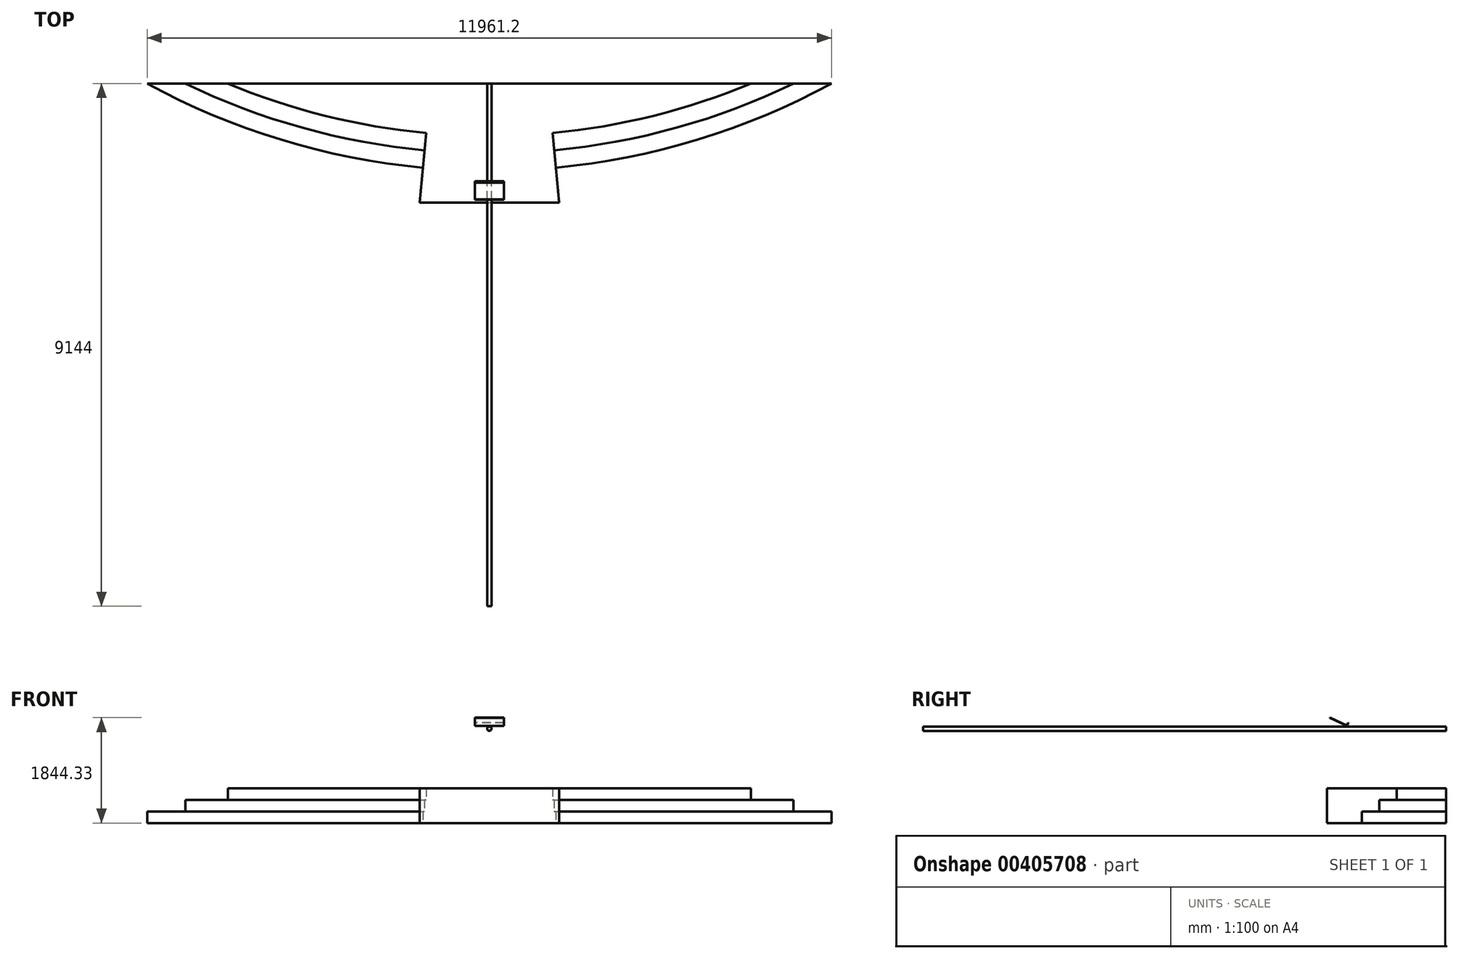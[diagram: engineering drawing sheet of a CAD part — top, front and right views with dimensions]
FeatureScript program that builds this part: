
annotation { "Feature Type Name" : "Feature", "Feature Type Description" : "" }
export const myFeature = defineFeature(function(context is Context, id is Id, definition is map)
    precondition{}
    {
        {
            var Q0;
            Q0=qCreatedBy(makeId("Top.planeOp"),FACE);
            var sketch = newSketch(context, id + "F0", { "sketchPlane" : qUnion([Q0])});
            skLineSegment(sketch, "E0", {"start": v(-4572, 0) * mm, "end": v(4572, 0) * mm});
            skArc(sketch, "E1", {"start": v(-4572, 0) * mm, "mid": v(0, -914.4) * mm, "end": v(4572, 0) * mm});
            skArc(sketch, "E2.0", {"start": v(-5314.37, 0) * mm, "mid": v(0, -1219.2) * mm, "end": v(5314.37, 0) * mm});
            skLineSegment(sketch, "E3", {"start": v(-4572, 0) * mm, "end": v(-5314.37, 0) * mm});
            skLineSegment(sketch, "E4", {"start": v(4572, 0) * mm, "end": v(5314.37, 0) * mm});
            skArc(sketch, "E5.0", {"start": v(-5980.6, 0) * mm, "mid": v(0, -1524) * mm, "end": v(5980.6, 0) * mm});
            skLineSegment(sketch, "E6", {"start": v(-5314.37, 0) * mm, "end": v(-5980.6, 0) * mm});
            skLineSegment(sketch, "E7", {"start": v(5314.37, 0) * mm, "end": v(5980.6, 0) * mm});
            skLineSegment(sketch, "E8", {"start": v(-1105.34, -862.9) * mm, "end": v(-1219.2, -2082.1) * mm});
            skLineSegment(sketch, "E9", {"start": v(-1219.2, -2082.1) * mm, "end": v(1219.2, -2082.1) * mm});
            skLineSegment(sketch, "E10", {"start": v(1219.2, -2082.1) * mm, "end": v(1105.34, -862.9) * mm});
            skLineSegment(sketch, "E11", {"start": v(0, -2082.1) * mm, "end": v(0, -1524) * mm});
            skSolve(sketch);
        }
        {
            var Q0;
            {var subQ0=sQuery(id+"F0.wireOp",EDGE,"E0");Q0=makeQuery(id+"F0.imprint","IMPRINT",FACE,{"disambiguationData":[TD([[makeQuery(id+"F0.imprint","IMPRINT",EDGE,{"derivedFrom":subQ0}),-1.0]])]});}
            var Q1;
            {var subQ0=sQuery(id+"F0.wireOp",EDGE,"E11");Q1=makeQuery(id+"F0.imprint","IMPRINT",FACE,{"disambiguationData":[TD([[makeQuery(id+"F0.imprint","IMPRINT",EDGE,{"derivedFrom":subQ0}),1.0]])]});}
            var Q2;
            {var subQ0=sQuery(id+"F0.wireOp",EDGE,"E11");Q2=makeQuery(id+"F0.imprint","IMPRINT",FACE,{"disambiguationData":[TD([[makeQuery(id+"F0.imprint","IMPRINT",EDGE,{"derivedFrom":subQ0}),-1.0]])]});}
            var Q3;
            {var subQ0=sQuery(id+"F0.wireOp",EDGE,"E8");var subQ3=sQuery(id+"F0.wireOp",EDGE,"E2.0");var subQ4=makeQuery(id+"F0.imprint","INTERSECT",VERTEX,{"derivedFrom":[subQ3,subQ0]});Q3=makeQuery(id+"F0.imprint","IMPRINT",FACE,{"disambiguationData":[TD([[makeQuery(id+"F0.imprint","IMPRINT",EDGE,{"disambiguationData":[TD([[subQ4,-1.0]])],"derivedFrom":subQ3}),-1.0]])]});}
            var Q4;
            {var subQ0=sQuery(id+"F0.wireOp",EDGE,"E8");var subQ1=sQuery(id+"F0.wireOp",EDGE,"E1");var subQ2=makeQuery(id+"F0.imprint","INTERSECT",VERTEX,{"derivedFrom":[subQ1,subQ0]});Q4=makeQuery(id+"F0.imprint","IMPRINT",FACE,{"disambiguationData":[TD([[makeQuery(id+"F0.imprint","IMPRINT",EDGE,{"disambiguationData":[TD([[subQ2,-1.0]])],"derivedFrom":subQ1}),-1.0]])]});}
            extrude(context, id + "F1", {"entities" : qUnion([Q0, Q1, Q2, Q3, Q4]), "depth" : 609.6 * mm});
        }
        {
            var Q0;
            {var subQ0=sQuery(id+"F0.wireOp",EDGE,"E3");Q0=makeQuery(id+"F0.imprint","IMPRINT",FACE,{"disambiguationData":[TD([[makeQuery(id+"F0.imprint","IMPRINT",EDGE,{"derivedFrom":subQ0}),1.0]])]});}
            var Q1;
            {var subQ0=sQuery(id+"F0.wireOp",EDGE,"E4");Q1=makeQuery(id+"F0.imprint","IMPRINT",FACE,{"disambiguationData":[TD([[makeQuery(id+"F0.imprint","IMPRINT",EDGE,{"derivedFrom":subQ0}),-1.0]])]});}
            extrude(context, id + "F2", {"entities" : qUnion([Q0, Q1]), "operationType" : NewBodyOperationType.ADD, "depth" : 406.4 * mm});
        }
        {
            var Q0;
            {var subQ0=sQuery(id+"F0.wireOp",EDGE,"E6");Q0=makeQuery(id+"F0.imprint","IMPRINT",FACE,{"disambiguationData":[TD([[makeQuery(id+"F0.imprint","IMPRINT",EDGE,{"derivedFrom":subQ0}),1.0]])]});}
            var Q1;
            {var subQ0=sQuery(id+"F0.wireOp",EDGE,"E7");Q1=makeQuery(id+"F0.imprint","IMPRINT",FACE,{"disambiguationData":[TD([[makeQuery(id+"F0.imprint","IMPRINT",EDGE,{"derivedFrom":subQ0}),-1.0]])]});}
            extrude(context, id + "F3", {"entities" : qUnion([Q0, Q1]), "operationType" : NewBodyOperationType.ADD, "depth" : 203.2 * mm});
        }
        {
            var Q0;
            Q0=qCreatedBy(makeId("Front.planeOp"),FACE);
            var sketch = newSketch(context, id + "F4", { "sketchPlane" : qUnion([Q0])});
            skLineSegment(sketch, "E12", {"start": v(0, 0) * mm, "end": v(0, 1651) * mm});
            skCircle(sketch, "E13", {"center": v(0, 1651) * mm, "radius": 38.1 * mm});
            skSolve(sketch);
        }
        {
            var Q0;
            Q0 = qSketchRegion(id + "F4", true);
            extrude(context, id + "F5", {"entities" : qUnion([Q0]), "depth" : 9144 * mm});
        }
        {
            var Q0;
            Q0=qCreatedBy(makeId("Right.planeOp"),FACE);
            var sketch = newSketch(context, id + "F6", { "sketchPlane" : qUnion([Q0])});
            skLineSegment(sketch, "E14", {"start": v(-1878.9, 626.95) * mm, "end": v(-1878.9, 1769.95) * mm});
            skLineSegment(sketch, "E15", {"start": v(-2028.53, 1839.73) * mm, "end": v(-1729.27, 1700.18) * mm});
            skLineSegment(sketch, "E16", {"start": v(-1729.27, 1700.18) * mm, "end": v(-1705.11, 1751.98) * mm});
            skLineSegment(sketch, "E17.0", {"start": v(-1731.72, 1706.93) * mm, "end": v(-1709.72, 1754.12) * mm});
            skLineSegment(sketch, "E17.1", {"start": v(-2026.38, 1844.33) * mm, "end": v(-1731.72, 1706.93) * mm});
            skLineSegment(sketch, "E18", {"start": v(-1705.11, 1751.98) * mm, "end": v(-1709.72, 1754.12) * mm});
            skLineSegment(sketch, "E19", {"start": v(-2028.53, 1839.73) * mm, "end": v(-2026.38, 1844.33) * mm});
            skSolve(sketch);
        }
        {
            var Q0;
            Q0 = qSketchRegion(id + "F6", true);
            extrude(context, id + "F7", {"entities" : qUnion([Q0]), "endBound" : BoundingType.SYMMETRIC, "depth" : 508 * mm});
        }
    });
